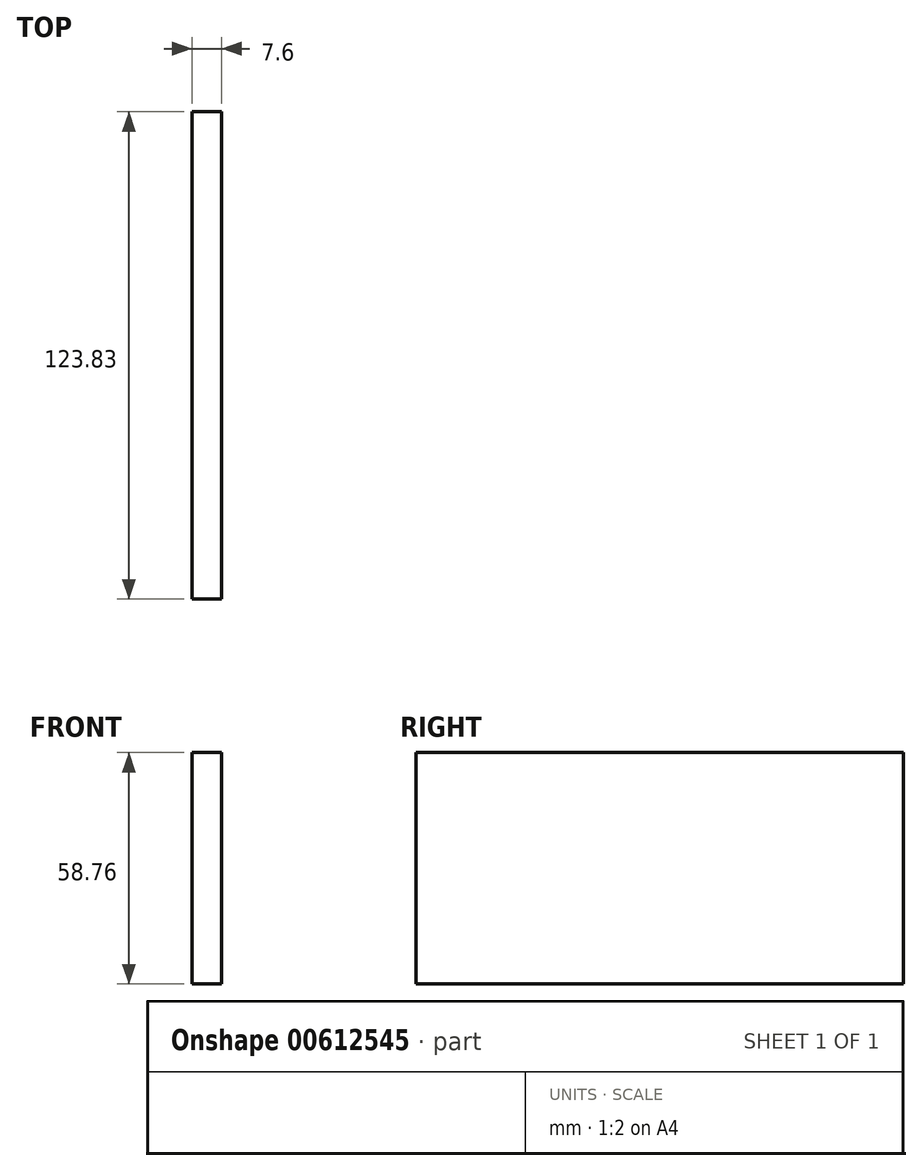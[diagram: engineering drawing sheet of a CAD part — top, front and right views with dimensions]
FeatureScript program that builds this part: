
annotation { "Feature Type Name" : "Feature", "Feature Type Description" : "" }
export const myFeature = defineFeature(function(context is Context, id is Id, definition is map)
    precondition{}
    {
        {
            var Q0;
            Q0=qCreatedBy(makeId("Top.planeOp"),FACE);
            var sketch = newSketch(context, id + "F0", { "sketchPlane" : qUnion([Q0])});
            skLineSegment(sketch, "E0", {"start": v(0, 0) * mm, "end": v(-7.6, 0) * mm});
            skLineSegment(sketch, "E1", {"start": v(-7.6, 0) * mm, "end": v(-7.6, 123.83) * mm});
            skLineSegment(sketch, "E2", {"start": v(0, 123.83) * mm, "end": v(0, 0) * mm});
            skLineSegment(sketch, "E3", {"start": v(0, 123.83) * mm, "end": v(-7.6, 123.83) * mm});
            skSolve(sketch);
        }
        {
            var Q0;
            Q0 = qSketchRegion(id + "F0", true);
            extrude(context, id + "F1", {"entities" : qUnion([Q0]), "endBound" : BoundingType.SYMMETRIC, "depth" : 58.75 * mm, "offsetDistance" : 25.4 * mm});
        }
    });
